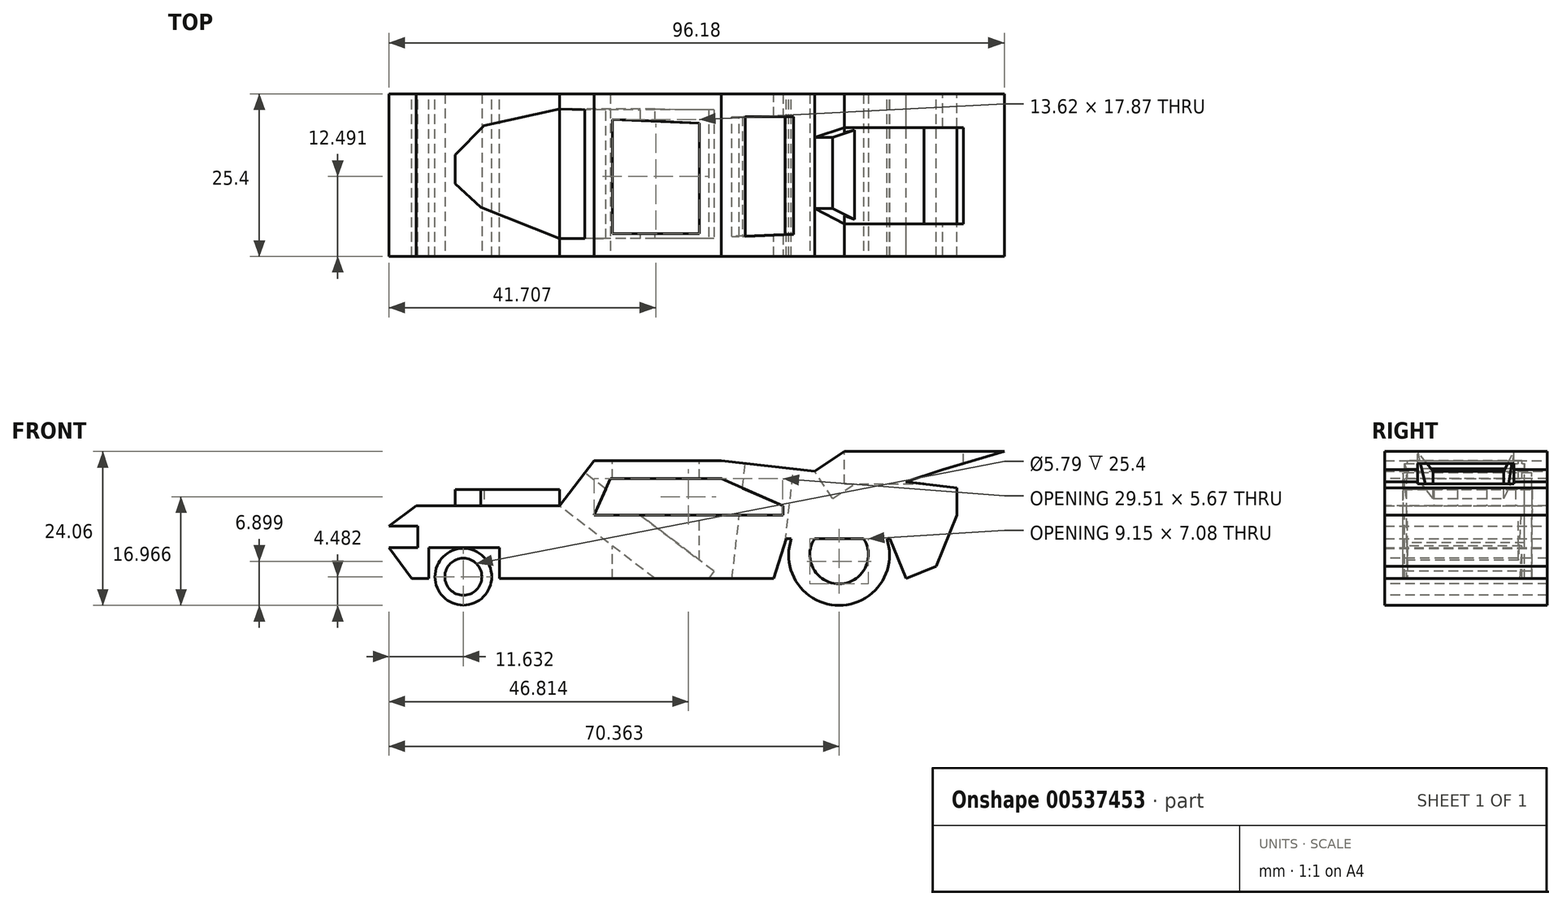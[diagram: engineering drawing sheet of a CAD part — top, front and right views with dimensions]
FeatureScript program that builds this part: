
annotation { "Feature Type Name" : "Feature", "Feature Type Description" : "" }
export const myFeature = defineFeature(function(context is Context, id is Id, definition is map)
    precondition{}
    {
        {
            var Q0;
            Q0=qCreatedBy(makeId("Front.planeOp"),FACE);
            var sketch = newSketch(context, id + "F0", { "sketchPlane" : qUnion([Q0])});
            skCircle(sketch, "E0", {"center": v(-28.8, 3.97) * mm, "radius": 4.43 * mm});
            skCircle(sketch, "E1", {"center": v(29.93, 7.38) * mm, "radius": 7.89 * mm});
            skSolve(sketch);
        }
        {
            var Q0;
            Q0=makeQuery(id+"F0.imprint","IMPRINT",FACE,{"disambiguationData":[TD([[makeQuery(id+"F0.imprint","IMPRINT",EDGE,{"derivedFrom":sQuery(id+"F0.wireOp",EDGE,"E0")}),1.0]])]});
            var Q1;
            Q1=makeQuery(id+"F0.imprint","IMPRINT",FACE,{"disambiguationData":[TD([[makeQuery(id+"F0.imprint","IMPRINT",EDGE,{"derivedFrom":sQuery(id+"F0.wireOp",EDGE,"E1")}),1.0]])]});
            extrude(context, id + "F1", {"entities" : qUnion([Q0, Q1]), "depth" : 25.4 * mm, "offsetDistance" : 25.4 * mm});
        }
        {
            var Q0;
            Q0=qCreatedBy(makeId("Front.planeOp"),FACE);
            var sketch = newSketch(context, id + "F2", { "sketchPlane" : qUnion([Q0])});
            skLineSegment(sketch, "E2", {"start": v(-23.12, 3.69) * mm, "end": v(19.72, 3.69) * mm});
            skLineSegment(sketch, "E3", {"start": v(19.72, 3.69) * mm, "end": v(21.7, 9.93) * mm});
            skLineSegment(sketch, "E4", {"start": v(21.7, 9.93) * mm, "end": v(37.88, 9.93) * mm});
            skLineSegment(sketch, "E5", {"start": v(37.88, 9.93) * mm, "end": v(40.43, 3.69) * mm});
            skLineSegment(sketch, "E6", {"start": v(40.43, 3.69) * mm, "end": v(45.1, 5.6) * mm});
            skLineSegment(sketch, "E7", {"start": v(45.1, 5.6) * mm, "end": v(48.37, 13.62) * mm});
            skLineSegment(sketch, "E8", {"start": v(48.37, 13.62) * mm, "end": v(48.37, 17.87) * mm});
            skLineSegment(sketch, "E9", {"start": v(48.37, 17.87) * mm, "end": v(11.5, 22.13) * mm});
            skLineSegment(sketch, "E10", {"start": v(11.5, 22.13) * mm, "end": v(-8.37, 22.13) * mm});
            skLineSegment(sketch, "E11", {"start": v(-8.37, 22.13) * mm, "end": v(-13.76, 15.04) * mm});
            skLineSegment(sketch, "E12", {"start": v(-13.76, 15.04) * mm, "end": v(-36.17, 15.04) * mm});
            skLineSegment(sketch, "E13", {"start": v(-36.17, 15.04) * mm, "end": v(-40.43, 11.92) * mm});
            skLineSegment(sketch, "E14", {"start": v(-40.43, 11.92) * mm, "end": v(-35.9, 11.92) * mm});
            skLineSegment(sketch, "E15", {"start": v(-35.9, 11.92) * mm, "end": v(-35.9, 8.51) * mm});
            skLineSegment(sketch, "E16", {"start": v(-35.9, 8.51) * mm, "end": v(-40.43, 8.51) * mm});
            skLineSegment(sketch, "E17", {"start": v(-40.43, 8.51) * mm, "end": v(-36.9, 3.69) * mm});
            skLineSegment(sketch, "E18", {"start": v(-36.9, 3.69) * mm, "end": v(-34.19, 3.69) * mm});
            skLineSegment(sketch, "E19", {"start": v(-34.19, 3.69) * mm, "end": v(-34.19, 8.51) * mm});
            skLineSegment(sketch, "E20", {"start": v(-34.19, 8.51) * mm, "end": v(-23.12, 8.51) * mm});
            skLineSegment(sketch, "E21", {"start": v(-23.12, 8.51) * mm, "end": v(-23.12, 3.69) * mm});
            skSolve(sketch);
        }
        {
            var Q0;
            Q0=makeQuery(id+"F2.imprint","IMPRINT",FACE,{"disambiguationData":[TD([[makeQuery(id+"F2.imprint","IMPRINT",EDGE,{"derivedFrom":sQuery(id+"F2.wireOp",EDGE,"E2")}),1.0]])]});
            extrude(context, id + "F3", {"entities" : qUnion([Q0]), "operationType" : NewBodyOperationType.ADD, "depth" : 25.4 * mm, "offsetDistance" : 25.4 * mm});
        }
        {
            var Q0;
            Q0=qCreatedBy(makeId("Front.planeOp"),FACE);
            var sketch = newSketch(context, id + "F4", { "sketchPlane" : qUnion([Q0])});
            skLineSegment(sketch, "E22", {"start": v(25.68, 20.14) * mm, "end": v(30.78, 23.55) * mm});
            skLineSegment(sketch, "E23", {"start": v(30.78, 23.55) * mm, "end": v(55.75, 23.55) * mm});
            skLineSegment(sketch, "E24", {"start": v(55.75, 23.55) * mm, "end": v(46.1, 20.71) * mm});
            skLineSegment(sketch, "E25", {"start": v(46.1, 20.71) * mm, "end": v(38.44, 18.16) * mm});
            skLineSegment(sketch, "E26", {"start": v(38.44, 18.16) * mm, "end": v(25.68, 20.14) * mm});
            skSolve(sketch);
        }
        {
            var Q0;
            Q0=makeQuery(id+"F4.imprint","IMPRINT",FACE,{"disambiguationData":[TD([[makeQuery(id+"F4.imprint","IMPRINT",EDGE,{"derivedFrom":sQuery(id+"F4.wireOp",EDGE,"E22")}),-1.0]])]});
            extrude(context, id + "F5", {"entities" : qUnion([Q0]), "operationType" : NewBodyOperationType.ADD, "depth" : 25.4 * mm, "offsetDistance" : 25.4 * mm});
        }
        {
            var Q0;
            Q0=makeQuery(id+"F5.boolean.opBoolean","MERGE",FACE,{"derivedFrom":[makeQuery(id+"F3.boolean.opBoolean","MERGE",FACE,{"derivedFrom":[makeQuery(id+"F1.opExtrude","CAP_FACE",FACE,{"disambiguationData":[OSD([sQuery(id+"F0.wireOp",EDGE,"E1")])],"isStart":false}),makeQuery(id+"F3.opExtrude","CAP_FACE",FACE,{"disambiguationData":[OSD([sQuery(id+"F2.wireOp",EDGE,"E2"),sQuery(id+"F2.wireOp",EDGE,"E3"),sQuery(id+"F2.wireOp",EDGE,"E4"),sQuery(id+"F2.wireOp",EDGE,"E5"),sQuery(id+"F2.wireOp",EDGE,"E6"),sQuery(id+"F2.wireOp",EDGE,"E7"),sQuery(id+"F2.wireOp",EDGE,"E8"),sQuery(id+"F2.wireOp",EDGE,"E9"),sQuery(id+"F2.wireOp",EDGE,"E10"),sQuery(id+"F2.wireOp",EDGE,"E11"),sQuery(id+"F2.wireOp",EDGE,"E12"),sQuery(id+"F2.wireOp",EDGE,"E13"),sQuery(id+"F2.wireOp",EDGE,"E14"),sQuery(id+"F2.wireOp",EDGE,"E15"),sQuery(id+"F2.wireOp",EDGE,"E16"),sQuery(id+"F2.wireOp",EDGE,"E17"),sQuery(id+"F2.wireOp",EDGE,"E18"),sQuery(id+"F2.wireOp",EDGE,"E19"),sQuery(id+"F2.wireOp",EDGE,"E20"),sQuery(id+"F2.wireOp",EDGE,"E21")])],"isStart":false})]}),makeQuery(id+"F5.opExtrude","CAP_FACE",FACE,{"disambiguationData":[OSD([sQuery(id+"F4.wireOp",EDGE,"E22"),sQuery(id+"F4.wireOp",EDGE,"E23"),sQuery(id+"F4.wireOp",EDGE,"E24"),sQuery(id+"F4.wireOp",EDGE,"E25"),sQuery(id+"F4.wireOp",EDGE,"E26")])],"isStart":false})]});
            var sketch = newSketch(context, id + "F6", { "sketchPlane" : qUnion([Q0])});
            skLineSegment(sketch, "E27", {"start": v(-8.37, 13.62) * mm, "end": v(-5.82, 19.3) * mm});
            skLineSegment(sketch, "E28", {"start": v(-5.82, 19.3) * mm, "end": v(11.5, 19.3) * mm});
            skLineSegment(sketch, "E29", {"start": v(11.5, 19.3) * mm, "end": v(21.14, 15.04) * mm});
            skLineSegment(sketch, "E30", {"start": v(21.14, 15.04) * mm, "end": v(21.14, 13.62) * mm});
            skLineSegment(sketch, "E31", {"start": v(21.14, 13.62) * mm, "end": v(-8.37, 13.62) * mm});
            skSolve(sketch);
        }
        {
            var Q0;
            Q0=makeQuery(id+"F6.imprint","IMPRINT",FACE,{"disambiguationData":[TD([[makeQuery(id+"F6.imprint","IMPRINT",EDGE,{"derivedFrom":sQuery(id+"F6.wireOp",EDGE,"E27")}),-1.0]])]});
            extrude(context, id + "F7", {"entities" : qUnion([Q0]), "operationType" : NewBodyOperationType.REMOVE, "oppositeDirection" : true, "depth" : 25.4 * mm, "offsetDistance" : 25.4 * mm});
        }
        {
            var Q0;
            Q0=makeQuery(id+"F3.opExtrude","SWEPT_FACE",FACE,{"disambiguationData":[OSD([sQuery(id+"F2.wireOp",EDGE,"E11")])]});
            var sketch = newSketch(context, id + "F8", { "sketchPlane" : qUnion([Q0])});
            skLineSegment(sketch, "E32", {"start": v(2.45, 10.13) * mm, "end": v(22.59, 10.13) * mm});
            skLineSegment(sketch, "E33", {"start": v(22.59, 10.13) * mm, "end": v(22.59, 3.65) * mm});
            skLineSegment(sketch, "E34", {"start": v(22.59, 3.65) * mm, "end": v(2.34, 3.65) * mm});
            skLineSegment(sketch, "E35", {"start": v(2.34, 3.65) * mm, "end": v(2.45, 10.13) * mm});
            skSolve(sketch);
        }
        {
            var Q0;
            Q0=makeQuery(id+"F8.imprint","IMPRINT",FACE,{"disambiguationData":[TD([[makeQuery(id+"F8.imprint","IMPRINT",EDGE,{"derivedFrom":sQuery(id+"F8.wireOp",EDGE,"E32")}),-1.0]])]});
            extrude(context, id + "F9", {"entities" : qUnion([Q0]), "operationType" : NewBodyOperationType.REMOVE, "oppositeDirection" : true, "depth" : 25.4 * mm, "offsetDistance" : 25.4 * mm});
        }
        {
            var Q0;
            {var subQ11=sQuery(id+"F2.wireOp",EDGE,"E10");var subQ12=sQuery(id+"F2.wireOp",EDGE,"E9");Q0=makeQuery(id+"F5.boolean.opBoolean","SPLIT",FACE,{"disambiguationData":[TD([makeQuery(id+"F3.opExtrude","SWEPT_FACE",FACE,{"disambiguationData":[OSD([subQ11])]})])],"derivedFrom":makeQuery(id+"F3.opExtrude","SWEPT_FACE",FACE,{"disambiguationData":[OSD([subQ12])]})});}
            var sketch = newSketch(context, id + "F10", { "sketchPlane" : qUnion([Q0])});
            skLineSegment(sketch, "E36", {"start": v(12.69, -22.27) * mm, "end": v(12.69, -3.55) * mm});
            skLineSegment(sketch, "E37", {"start": v(12.69, -3.55) * mm, "end": v(20.3, -3.55) * mm});
            skLineSegment(sketch, "E38", {"start": v(20.3, -3.55) * mm, "end": v(20.3, -21.99) * mm});
            skLineSegment(sketch, "E39", {"start": v(20.3, -21.99) * mm, "end": v(12.69, -22.27) * mm});
            skSolve(sketch);
        }
        {
            var Q0;
            Q0=makeQuery(id+"F10.imprint","IMPRINT",FACE,{"disambiguationData":[TD([[makeQuery(id+"F10.imprint","IMPRINT",EDGE,{"derivedFrom":sQuery(id+"F10.wireOp",EDGE,"E36")}),-1.0]])]});
            extrude(context, id + "F11", {"entities" : qUnion([Q0]), "operationType" : NewBodyOperationType.REMOVE, "oppositeDirection" : true, "depth" : 25.4 * mm, "offsetDistance" : 25.4 * mm});
        }
        {
            var Q0;
            Q0=makeQuery(id+"F3.opExtrude","SWEPT_FACE",FACE,{"disambiguationData":[OSD([sQuery(id+"F2.wireOp",EDGE,"E10")])]});
            var sketch = newSketch(context, id + "F12", { "sketchPlane" : qUnion([Q0])});
            skLineSegment(sketch, "E40", {"start": v(-5.53, -3.97) * mm, "end": v(-5.53, -21.85) * mm});
            skLineSegment(sketch, "E41", {"start": v(-5.53, -21.85) * mm, "end": v(8.09, -21.85) * mm});
            skLineSegment(sketch, "E42", {"start": v(8.09, -21.85) * mm, "end": v(8.09, -4.54) * mm});
            skLineSegment(sketch, "E43", {"start": v(8.09, -4.54) * mm, "end": v(-5.53, -3.97) * mm});
            skSolve(sketch);
        }
        {
            var Q0;
            Q0=makeQuery(id+"F12.imprint","IMPRINT",FACE,{"disambiguationData":[TD([[makeQuery(id+"F12.imprint","IMPRINT",EDGE,{"derivedFrom":sQuery(id+"F12.wireOp",EDGE,"E40")}),1.0]])]});
            extrude(context, id + "F13", {"entities" : qUnion([Q0]), "operationType" : NewBodyOperationType.REMOVE, "oppositeDirection" : true, "depth" : 25.4 * mm, "offsetDistance" : 25.4 * mm});
        }
        {
            var Q0;
            Q0=makeQuery(id+"F1.opExtrude","CAP_FACE",FACE,{"disambiguationData":[OSD([sQuery(id+"F0.wireOp",EDGE,"E0")])],"isStart":false});
            var sketch = newSketch(context, id + "F14", { "sketchPlane" : qUnion([Q0])});
            skCircle(sketch, "E44", {"center": v(-28.8, 3.97) * mm, "radius": 2.9 * mm});
            skSolve(sketch);
        }
        {
            var Q0;
            Q0=makeQuery(id+"F14.imprint","IMPRINT",FACE,{"disambiguationData":[TD([[makeQuery(id+"F14.imprint","IMPRINT",EDGE,{"derivedFrom":sQuery(id+"F14.wireOp",EDGE,"E44")}),1.0]])]});
            extrude(context, id + "F15", {"entities" : qUnion([Q0]), "operationType" : NewBodyOperationType.REMOVE, "oppositeDirection" : true, "depth" : 25.4 * mm, "offsetDistance" : 25.4 * mm});
        }
        {
            var Q0;
            Q0=makeQuery(id+"F3.opExtrude","SWEPT_FACE",FACE,{"disambiguationData":[OSD([sQuery(id+"F2.wireOp",EDGE,"E12")])]});
            var sketch = newSketch(context, id + "F16", { "sketchPlane" : qUnion([Q0])});
            skLineSegment(sketch, "E45", {"start": v(-13.76, -2.34) * mm, "end": v(-25.54, -4.97) * mm});
            skLineSegment(sketch, "E46", {"start": v(-25.54, -4.97) * mm, "end": v(-30.07, -9.5) * mm});
            skLineSegment(sketch, "E47", {"start": v(-30.07, -9.5) * mm, "end": v(-30.07, -14.04) * mm});
            skLineSegment(sketch, "E48", {"start": v(-30.07, -14.04) * mm, "end": v(-26.1, -17.73) * mm});
            skLineSegment(sketch, "E49", {"start": v(-26.1, -17.73) * mm, "end": v(-13.76, -22.59) * mm});
            skSolve(sketch);
        }
        {
            var Q0;
            Q0=makeQuery(id+"F16.imprint","IMPRINT",FACE,{"disambiguationData":[TD([[makeQuery(id+"F16.imprint","IMPRINT",EDGE,{"derivedFrom":sQuery(id+"F16.wireOp",EDGE,"E45")}),1.0]])]});
            extrude(context, id + "F17", {"entities" : qUnion([Q0]), "operationType" : NewBodyOperationType.ADD, "depth" : 2.54 * mm, "offsetDistance" : 25.4 * mm});
        }
        {
            var Q0;
            Q0=makeQuery(id+"F5.opExtrude","SWEPT_FACE",FACE,{"disambiguationData":[OSD([sQuery(id+"F4.wireOp",EDGE,"E23")])]});
            var sketch = newSketch(context, id + "F18", { "sketchPlane" : qUnion([Q0])});
            skLineSegment(sketch, "E50", {"start": v(30.78, -20.29) * mm, "end": v(49.37, -20.29) * mm});
            skLineSegment(sketch, "E51", {"start": v(49.37, -20.29) * mm, "end": v(49.37, -5.25) * mm});
            skLineSegment(sketch, "E52", {"start": v(49.37, -5.25) * mm, "end": v(30.78, -5.25) * mm});
            skLineSegment(sketch, "E53", {"start": v(30.78, -5.25) * mm, "end": v(30.78, -20.29) * mm});
            skSolve(sketch);
        }
        {
            var Q0;
            Q0=makeQuery(id+"F18.imprint","IMPRINT",FACE,{"disambiguationData":[TD([[makeQuery(id+"F18.imprint","IMPRINT",EDGE,{"derivedFrom":sQuery(id+"F18.wireOp",EDGE,"E50")}),1.0]])]});
            extrude(context, id + "F19", {"entities" : qUnion([Q0]), "operationType" : NewBodyOperationType.ADD, "depth" : 5.08 * mm, "offsetDistance" : 25.4 * mm});
        }
        {
            var Q0;
            Q0=makeQuery(id+"F19.opExtrude","CAP_FACE",FACE,{"disambiguationData":[OSD([sQuery(id+"F18.wireOp",EDGE,"E50"),sQuery(id+"F18.wireOp",EDGE,"E51"),sQuery(id+"F18.wireOp",EDGE,"E52"),sQuery(id+"F18.wireOp",EDGE,"E53")])],"isStart":false});
            extrude(context, id + "F20", {"entities" : qUnion([Q0]), "operationType" : NewBodyOperationType.REMOVE, "oppositeDirection" : true, "depth" : 10.16 * mm, "offsetDistance" : 25.4 * mm});
        }
        {
            var Q0;
            Q0=makeQuery(id+"F5.opExtrude","SWEPT_FACE",FACE,{"disambiguationData":[OSD([sQuery(id+"F4.wireOp",EDGE,"E22")])]});
            var sketch = newSketch(context, id + "F21", { "sketchPlane" : qUnion([Q0])});
            skLineSegment(sketch, "E54", {"start": v(33.08, -6.8) * mm, "end": v(38.68, -5.25) * mm});
            skLineSegment(sketch, "E55", {"start": v(38.68, -5.25) * mm, "end": v(38.68, -20.29) * mm});
            skLineSegment(sketch, "E56", {"start": v(33.08, -17.87) * mm, "end": v(38.68, -20.29) * mm});
            skLineSegment(sketch, "E57", {"start": v(33.08, -17.87) * mm, "end": v(33.08, -6.8) * mm});
            skSolve(sketch);
        }
        {
            var Q0;
            Q0=makeQuery(id+"F21.imprint","IMPRINT",FACE,{"disambiguationData":[TD([[makeQuery(id+"F21.imprint","IMPRINT",EDGE,{"derivedFrom":sQuery(id+"F21.wireOp",EDGE,"E54")}),-1.0]])]});
            extrude(context, id + "F22", {"entities" : qUnion([Q0]), "operationType" : NewBodyOperationType.REMOVE, "oppositeDirection" : true, "depth" : 5.08 * mm, "offsetDistance" : 25.4 * mm});
        }
        {
            var Q0;
            Q0=makeQuery(id+"F5.boolean.opBoolean","MERGE",FACE,{"derivedFrom":[makeQuery(id+"F3.boolean.opBoolean","MERGE",FACE,{"derivedFrom":[makeQuery(id+"F1.opExtrude","CAP_FACE",FACE,{"disambiguationData":[OSD([sQuery(id+"F0.wireOp",EDGE,"E1")])],"isStart":false}),makeQuery(id+"F3.opExtrude","CAP_FACE",FACE,{"disambiguationData":[OSD([sQuery(id+"F2.wireOp",EDGE,"E2"),sQuery(id+"F2.wireOp",EDGE,"E3"),sQuery(id+"F2.wireOp",EDGE,"E4"),sQuery(id+"F2.wireOp",EDGE,"E5"),sQuery(id+"F2.wireOp",EDGE,"E6"),sQuery(id+"F2.wireOp",EDGE,"E7"),sQuery(id+"F2.wireOp",EDGE,"E8"),sQuery(id+"F2.wireOp",EDGE,"E9"),sQuery(id+"F2.wireOp",EDGE,"E10"),sQuery(id+"F2.wireOp",EDGE,"E11"),sQuery(id+"F2.wireOp",EDGE,"E12"),sQuery(id+"F2.wireOp",EDGE,"E13"),sQuery(id+"F2.wireOp",EDGE,"E14"),sQuery(id+"F2.wireOp",EDGE,"E15"),sQuery(id+"F2.wireOp",EDGE,"E16"),sQuery(id+"F2.wireOp",EDGE,"E17"),sQuery(id+"F2.wireOp",EDGE,"E18"),sQuery(id+"F2.wireOp",EDGE,"E19"),sQuery(id+"F2.wireOp",EDGE,"E20"),sQuery(id+"F2.wireOp",EDGE,"E21")])],"isStart":false})]}),makeQuery(id+"F5.opExtrude","CAP_FACE",FACE,{"disambiguationData":[OSD([sQuery(id+"F4.wireOp",EDGE,"E22"),sQuery(id+"F4.wireOp",EDGE,"E23"),sQuery(id+"F4.wireOp",EDGE,"E24"),sQuery(id+"F4.wireOp",EDGE,"E25"),sQuery(id+"F4.wireOp",EDGE,"E26")])],"isStart":false})]});
            var sketch = newSketch(context, id + "F23", { "sketchPlane" : qUnion([Q0])});
            skArc(sketch, "E58", {"start": v(26.1, 9.93) * mm, "mid": v(29.93, 2.85) * mm, "end": v(33.76, 9.93) * mm});
            skLineSegment(sketch, "E59", {"start": v(26.1, 9.93) * mm, "end": v(33.76, 9.93) * mm});
            skSolve(sketch);
        }
        {
            var Q0;
            Q0=makeQuery(id+"F23.imprint","IMPRINT",FACE,{"disambiguationData":[TD([[makeQuery(id+"F23.imprint","IMPRINT",EDGE,{"derivedFrom":sQuery(id+"F23.wireOp",EDGE,"E58")}),1.0]])]});
            extrude(context, id + "F24", {"entities" : qUnion([Q0]), "operationType" : NewBodyOperationType.REMOVE, "oppositeDirection" : true, "depth" : 25.4 * mm, "offsetDistance" : 25.4 * mm});
        }
    });
